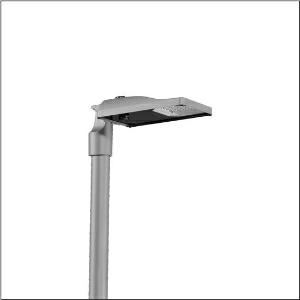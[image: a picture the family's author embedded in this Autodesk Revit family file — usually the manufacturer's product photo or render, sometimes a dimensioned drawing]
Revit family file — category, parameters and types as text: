
# Revit family: streetlight_sl_31_micro___st0_5a_5xh5b31t08da_db8b
name_source: partatom
category: Lighting Fixtures
units: mm (PartAtom-declared; Revit-internal decimal feet)

## family parameters
Cut with Voids When Loaded = No
Host = Face
Light Source = No
Part Type = Normal
Room Calculation Point = No
Round Connector Dimension = Use Diameter
Shared = No

## types (1)
- --- (1 x LED, 4940 lm, 37.7 W, 3000K)
    Apparent Load = 38 VA
    CIE Flux Codes = 41 75 97 100 100
    Color Rendering = 70
    Color Temperature = 3000K
    Default Elevation = 1800 mm
    Description = Streetlight SL 31 micro D4i, Desk-Remote mast luminaire for post-top, side-entry; light control with lens of PMMA; light distribution: ST0.5a, direct asymmetric distribution, for standard-compliant lighting for roads and squares; LED: luminous flux: 4.940lm, light colour: 730, colour temperature: 3000K; luminous efficacy: 131lm/W; control: pre-setting: logarithmic dimming characteristic, flexible luminous flux parameterisation, time-dependent luminous flux control, constant luminous flux control, power reduction, intelligent temperature release in ECG and LED module, overheat protection; luminaire housing, of diecast aluminium, SITECO metallic grey (DB 702S), corrosivity category C5 high according to DIN EN ISO 12944; cover of toughened safety glass, transparent, opened without tools; mast flange of diecast aluminium, SITECO metallic grey (DB 702S), spigot size: 76/60mm, mast flange included unmounted; with cable H07RN-F 2x 1.5mm², cable length: 6,5m, connection cable pre-assembled; mains connection: 220..240V, AC, 50/60Hz; power consumption (at start of service life): 37,7W / (at end of service life): 40,9W / (with reduced operation 50%): 16,3W; protection rating (complete): IP66; insulation class (complete): insulation class II (safety insulation); impact resistance: IK09; certification: CE, ENEC, ENEC+, VDE, UKCA, ZD4i; permissible operating ambient temperature for outdoor applications: -40..+50°C; packaging unit: 1 piece

Light Distribution: ST0.5a
    Height = 76 mm
    Lamp = 1 x LED
    Lamp Light Flux = 4940 lm
    Lamp Power = 37.7 W
    Lamp count = 1
    Length = 467 mm
    Luminous efficacy = 131 lm/W
    Manufacturer = Siteco
    ModVariant = No
    Model = 5XH5B31T08DA
    Mounting Place = Pole
    Mounting Type = Pole top
    Number of Poles = 1
    OnlyDefault = Yes
    Power Factor = 1
    Product Name = Streetlight SL 31 micro | ST0.5a
    Product group = mast luminaire | pylon top
    ProductGroupID = 6100
    Protection Class = Protection class II
    Protection Degree = IP 66
    RLX_Detail_Level = 1
    RLX_Emergency_Light_Flux = 0 lm
    RLX_Emergency_Type = 0
    RLX_Emergency_Type_DB = No
    RlxData = <blob elided: 55141 chars, md5=5301bb6b>
    Socket = socket
    Standby Power = 0 W
    System Light Flux = 4940 lm
    System Power = 38 W
    Type Comments = factory setting: luminous flux: 100 % | dim-lin: 254 | 745 mA
    Type Image = l_1300315.jpg
    URL = http://relux.com
    VarID = @adj_057143
    Voltage = 0 V
    Weight = 0.00 kg
    Width = 265 mm

## geometry (parser evidence)
native form markers: Blend x4, Sweep x11
no freeform markers — native parametric forms only
